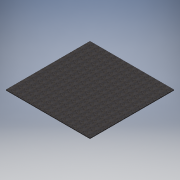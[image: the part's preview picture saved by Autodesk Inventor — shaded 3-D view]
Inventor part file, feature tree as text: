
AUTODESK INVENTOR PART (.ipt)
format: ipt  version: 2016 (Build 200138000, 138)  size: 102,400 bytes
history: native  units: in
note: dims shown in document units (in); Inventor stores cm internally (conversion verified against a paired STEP export)
features: extrude x1, sketch x1
ambient origin geometry x8: Origin, YZ Plane, XZ Plane, XY Plane, X Axis, Y Axis, Z Axis, Center Point
bodies: Solid1 (feature_tree)
feature tree (2):
  extrude  "Extrusion1"  Depth=1.0in TaperAngle=0.0deg
  sketch  "Sketch1"  dims[d0=108.0in d1=1.0in d2=0.0in]
